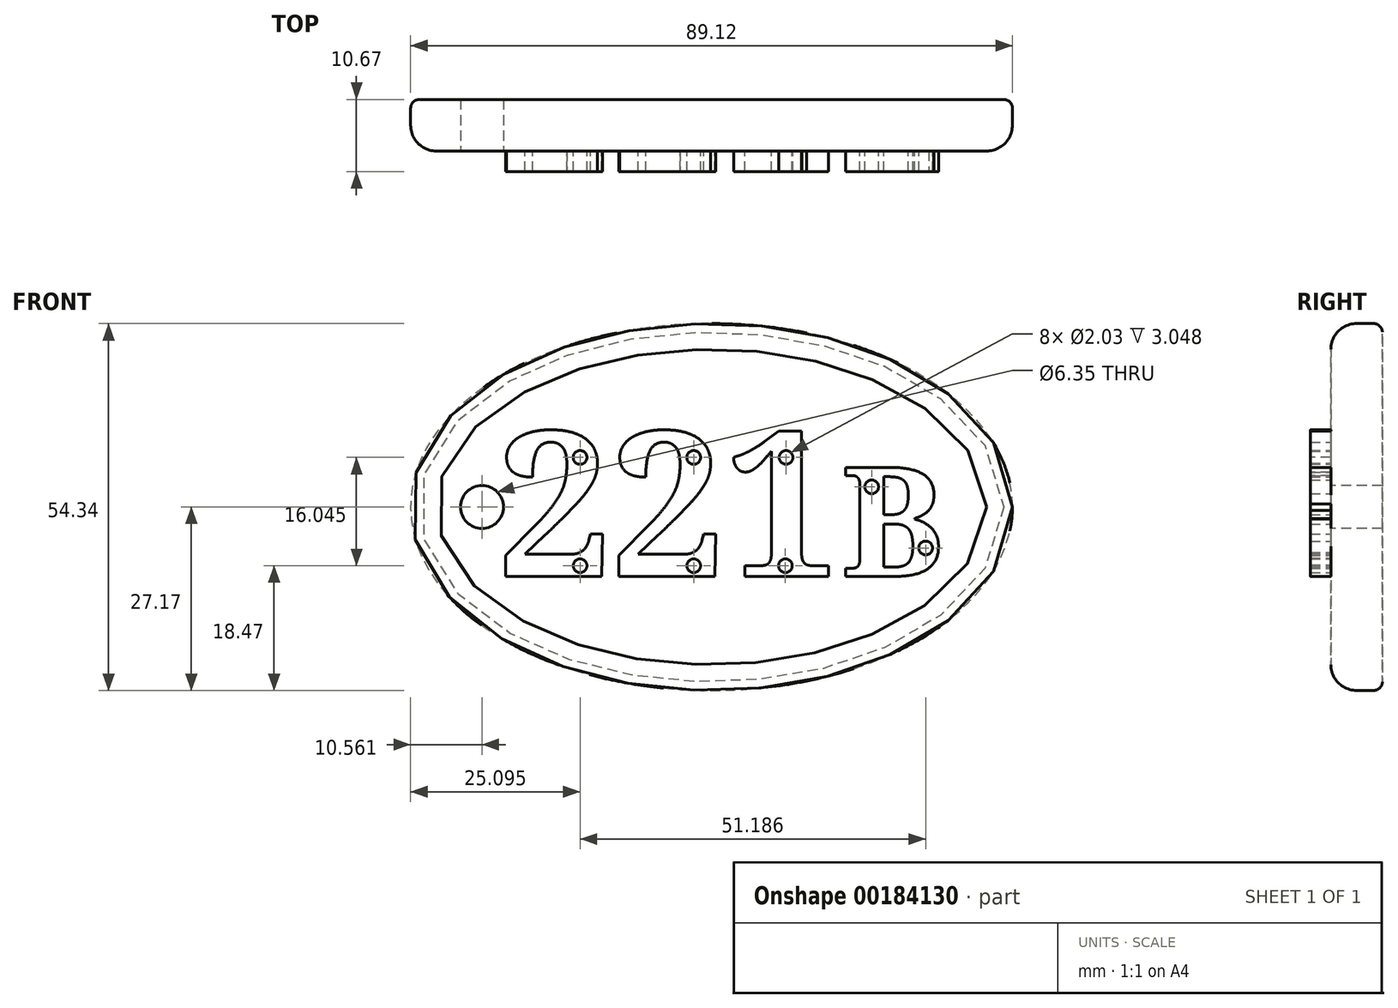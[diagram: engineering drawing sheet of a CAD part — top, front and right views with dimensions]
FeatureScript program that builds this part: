
annotation { "Feature Type Name" : "Feature", "Feature Type Description" : "" }
export const myFeature = defineFeature(function(context is Context, id is Id, definition is map)
    precondition{}
    {
        {
            var Q0;
            Q0=qCreatedBy(makeId("Front.planeOp"),FACE);
            var sketch = newSketch(context, id + "F0", { "sketchPlane" : qUnion([Q0])});
            skEllipse(sketch, "E0", {"center": v(0, 0) * mm, "majorRadius": 44.56 * mm, "minorRadius": 27.17 * mm, "majorAxis": v(1, 0)});
            skSolve(sketch);
        }
        {
            var Q0;
            Q0 = qSketchRegion(id + "F0", true);
            extrude(context, id + "F1", {"entities" : qUnion([Q0]), "endBound" : BoundingType.SYMMETRIC, "depth" : 7.62 * mm});
        }
        {
            var Q0;
            Q0=makeQuery(id+"F1.opExtrude","CAP_FACE",FACE,{"disambiguationData":[OSD([sQuery(id+"F0.wireOp",EDGE,"E0")])],"isStart":false});
            fillet(context, id + "F2", {"entities" : qUnion([Q0]), "radius" : 3.8 * mm, "tangentPropagation" : true, "allowEdgeOverflow" : false});
        }
        {
            var Q0;
            Q0=makeQuery(id+"F1.opExtrude","CAP_FACE",FACE,{"disambiguationData":[OSD([sQuery(id+"F0.wireOp",EDGE,"E0")])],"isStart":false});
            var sketch = newSketch(context, id + "F3", { "sketchPlane" : qUnion([Q0])});
            skText(sketch, "E1", { "text": "221", "fontName": "NotoSerif-Bold.ttf"});
            skText(sketch, "E2", { "text": "B", "fontName": "NotoSerif-Bold.ttf"});
            skCircle(sketch, "E3", {"center": v(-19.47, 7.35) * mm, "radius": 1.02 * mm});
            skCircle(sketch, "E4", {"center": v(-19.47, -8.7) * mm, "radius": 1.02 * mm});
            skCircle(sketch, "E5", {"center": v(-2.63, 7.35) * mm, "radius": 1.02 * mm});
            skCircle(sketch, "E6", {"center": v(-2.63, -8.7) * mm, "radius": 1.02 * mm});
            skCircle(sketch, "E7", {"center": v(10.94, -8.7) * mm, "radius": 1.02 * mm});
            skCircle(sketch, "E8", {"center": v(11.05, 7.35) * mm, "radius": 1.02 * mm});
            skCircle(sketch, "E9", {"center": v(23.72, 2.98) * mm, "radius": 1.02 * mm});
            skCircle(sketch, "E10", {"center": v(31.72, -6.07) * mm, "radius": 1.02 * mm});
            const initialGuessF3  = {"E1": [-0.03152, -0.01028, 1, 0, 0.02159], "E2": [0.01924, -0.01028, 1, 0, 0.01628]};
            skSetInitialGuess(sketch, initialGuessF3);
            skSolve(sketch);
        }
        {
            var Q0;
            Q0=makeQuery(id+"F3.imprint","IMPRINT",FACE,{"disambiguationData":[TD([[makeQuery(id+"F3.imprint","IMPRINT",EDGE,{"derivedFrom":sQuery(id+"F3.wireOp",EDGE,"E1.sketch_text.stroke-0")}),-1.0]])]});
            var Q1;
            Q1=makeQuery(id+"F3.imprint","IMPRINT",FACE,{"disambiguationData":[TD([[makeQuery(id+"F3.imprint","IMPRINT",EDGE,{"derivedFrom":sQuery(id+"F3.wireOp",EDGE,"E1.sketch_text.stroke-36")}),-1.0]])]});
            var Q2;
            Q2=makeQuery(id+"F3.imprint","IMPRINT",FACE,{"disambiguationData":[TD([[makeQuery(id+"F3.imprint","IMPRINT",EDGE,{"derivedFrom":sQuery(id+"F3.wireOp",EDGE,"E1.sketch_text.stroke-72")}),-1.0]])]});
            var Q3;
            Q3=makeQuery(id+"F3.imprint","IMPRINT",FACE,{"disambiguationData":[TD([[makeQuery(id+"F3.imprint","IMPRINT",EDGE,{"derivedFrom":sQuery(id+"F3.wireOp",EDGE,"E2.sketch_text.stroke-0")}),-1.0]])]});
            var Q4;
            Q4 = qSketchRegion(id + "F8", true);
            extrude(context, id + "F4", {"entities" : qUnion([Q0, Q1, Q2, Q3, Q4]), "operationType" : NewBodyOperationType.ADD, "depth" : 3.05 * mm});
        }
        {
            var Q0;
            Q0=makeQuery(id+"F3.imprint","IMPRINT",FACE,{"disambiguationData":[TD([[makeQuery(id+"F3.imprint","IMPRINT",EDGE,{"derivedFrom":sQuery(id+"F3.wireOp",EDGE,"E1.sketch_text.stroke-0")}),1.0]])]});
            var sketch = newSketch(context, id + "F5", { "sketchPlane" : qUnion([Q0])});
            skCircle(sketch, "E11", {"center": v(-34.44, 0) * mm, "radius": 2.57 * mm});
            skSolve(sketch);
        }
        {
            var Q0;
            Q0 = qSketchRegion(id + "F5", true);
            extrude(context, id + "F6", {"entities" : qUnion([Q0]), "operationType" : NewBodyOperationType.ADD, "oppositeDirection" : true, "depth" : 12.7 * mm});
        }
        {
            var Q0;
            Q0=makeQuery(id+"F1.opExtrude","CAP_EDGE",EDGE,{"disambiguationData":[OSD([sQuery(id+"F0.wireOp",EDGE,"E0")])],"isStart":true});
            fillet(context, id + "F7", {"entities" : qUnion([Q0]), "radius" : 1.27 * mm, "tangentPropagation" : true, "allowEdgeOverflow" : false});
        }
        {
            var Q0;
            Q0=makeQuery(id+"F3.imprint","IMPRINT",FACE,{"disambiguationData":[TD([[makeQuery(id+"F3.imprint","IMPRINT",EDGE,{"derivedFrom":sQuery(id+"F3.wireOp",EDGE,"E1.sketch_text.stroke-0")}),1.0]])]});
            var sketch = newSketch(context, id + "F8", { "sketchPlane" : qUnion([Q0])});
            skCircle(sketch, "E12", {"center": v(-34, 0) * mm, "radius": 3.17 * mm});
            skSolve(sketch);
        }
        {
            var Q0;
            Q0=sQuery(id+"F8.wireOp",VERTEX,"E12.center");
            var Q1;
            Q1=makeQuery(id+"F1.opExtrude","SWEPT_BODY",BODY,{"disambiguationData":[OSD([sQuery(id+"F0.wireOp",EDGE,"E0")])]});
            hole(context, id + "F9", {"style" : HoleStyle.SIMPLE, "endStyle" : HoleEndStyle.THROUGH, "holeDiameter" : 6.35 * mm, "locations" : qUnion([Q0]), "scope" : qUnion([Q1]), "isTappedThrough" : true});
        }
    });
